FCSTD DOCUMENT  (FreeCAD 1.0R39109 (Git))
Label: Plateau
License: All rights reserved
LicenseURL: https://en.wikipedia.org/wiki/All_rights_reserved
objects: Sketcher::SketchObject×1, PartDesign::Body×1
note: 3 computed .brp shape members not serialized (recipe doc carries the construction recipe); baked Part::Feature solids carry a one-line shape summary decoded from their .brp

FEATURE [Sketcher::SketchObject] Sketch
  ArcFitTolerance = 1e-06
  AttachmentSupport = -> [XZ_Plane]
  FullyConstrained = false
  MakeInternals = false
  MapMode = 5
  Placement = pos=(0,0,0) rot=(1,0,0;1.5708rad)
  sketch-geometry (4):
    g0: LineSegment StartX=-508.808 StartY=246.736 StartZ=0 EndX=-508.808 EndY=-653.264 EndZ=0
    g1: LineSegment StartX=-508.808 StartY=-653.264 StartZ=0 EndX=1291.19 EndY=-653.264 EndZ=0
    g2: LineSegment StartX=1291.19 StartY=-653.264 StartZ=0 EndX=1291.19 EndY=246.736 EndZ=0
    g3: LineSegment StartX=1291.19 StartY=246.736 StartZ=0 EndX=-508.808 EndY=246.736 EndZ=0
  constraints (10):
    c: Coincident(g0,g1)
    c: Coincident(g1,g2)
    c: Coincident(g2,g3)
    c: Coincident(g3,g0)
    c: Vertical(g0)
    c: Vertical(g2)
    c: Horizontal(g1)
    c: Horizontal(g3)
    c: DistanceX(g3,g3) = 1800  'largeur'
    c: DistanceY(g0,g0) = 900
FEATURE [PartDesign::Body] Body  label="Corps"
  AllowCompound = false
  Group = -> [Sketch]
  Origin = -> Origin
